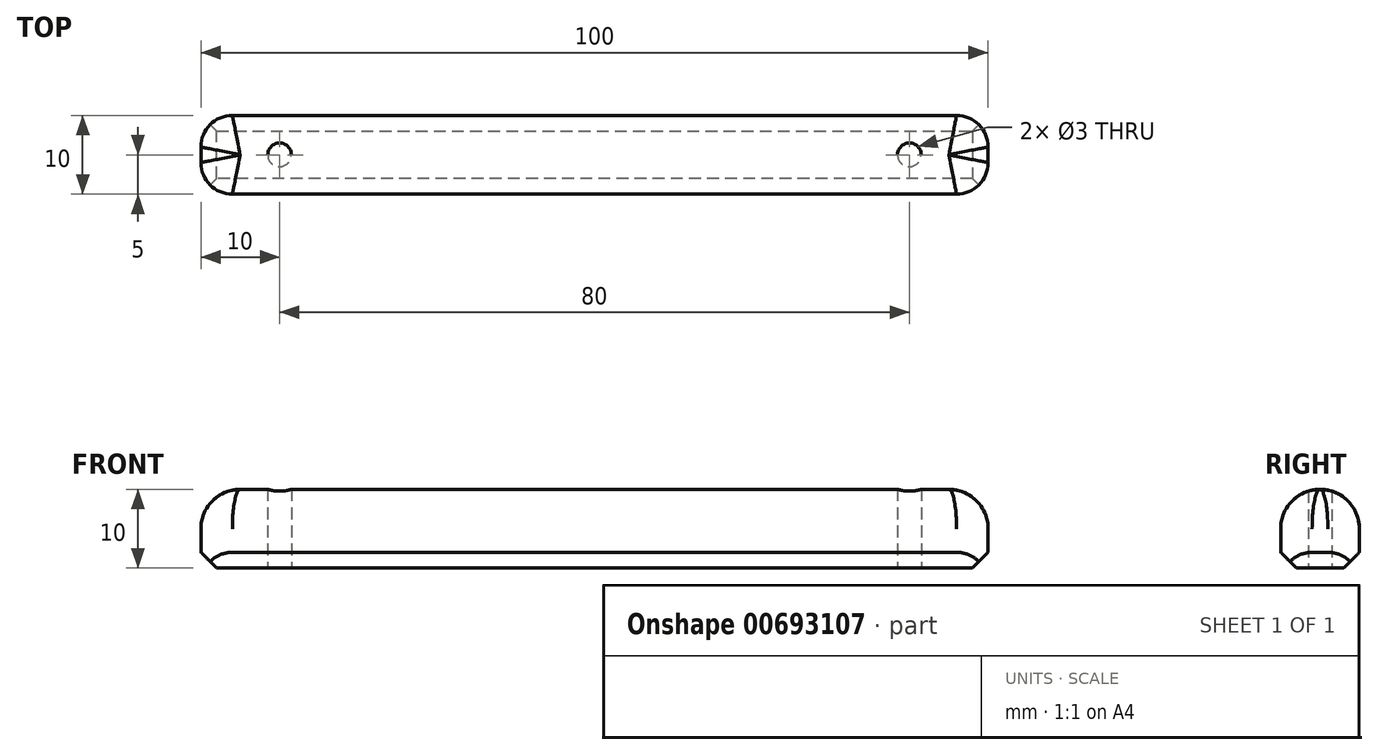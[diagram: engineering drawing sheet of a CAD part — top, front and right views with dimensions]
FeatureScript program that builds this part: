
annotation { "Feature Type Name" : "Feature", "Feature Type Description" : "" }
export const myFeature = defineFeature(function(context is Context, id is Id, definition is map)
    precondition{}
    {
        {
            var Q0;
            Q0=qCreatedBy(makeId("Top.planeOp"),FACE);
            var sketch = newSketch(context, id + "F0", { "sketchPlane" : qUnion([Q0])});
            skLineSegment(sketch, "E0.bottom", {"start": v(-50, 5) * mm, "end": v(50, 5) * mm});
            skLineSegment(sketch, "E0.top", {"start": v(-50, -5) * mm, "end": v(50, -5) * mm});
            skLineSegment(sketch, "E0.left", {"start": v(-50, 5) * mm, "end": v(-50, -5) * mm});
            skLineSegment(sketch, "E0.right", {"start": v(50, 5) * mm, "end": v(50, -5) * mm});
            skPoint(sketch, "E0.middle", {"position": v(0, 0) * mm});
            skSolve(sketch);
        }
        {
            var Q0;
            Q0 = qSketchRegion(id + "F0", true);
            extrude(context, id + "F1", {"entities" : qUnion([Q0]), "depth" : 10 * mm, "offsetDistance" : 25 * mm});
        }
        {
            var Q0;
            Q0=qCreatedBy(makeId("Top.planeOp"),FACE);
            var sketch = newSketch(context, id + "F2", { "sketchPlane" : qUnion([Q0])});
            skCircle(sketch, "E1", {"center": v(-40, 0) * mm, "radius": 1.5 * mm});
            skCircle(sketch, "E2", {"center": v(40, 0) * mm, "radius": 1.5 * mm});
            skSolve(sketch);
        }
        {
            var Q0;
            Q0 = qSketchRegion(id + "F2", true);
            extrude(context, id + "F3", {"entities" : qUnion([Q0]), "operationType" : NewBodyOperationType.REMOVE, "depth" : 10 * mm, "offsetDistance" : 25 * mm});
        }
        {
            var Q0;
            Q0=makeQuery(id+"F1.opExtrude","CAP_EDGE",EDGE,{"disambiguationData":[OSD([sQuery(id+"F0.wireOp",EDGE,"E0.top")])],"isStart":true});
            var Q1;
            Q1=makeQuery(id+"F1.opExtrude","CAP_EDGE",EDGE,{"disambiguationData":[OSD([sQuery(id+"F0.wireOp",EDGE,"E0.bottom")])],"isStart":true});
            var Q2;
            Q2=makeQuery(id+"F1.opExtrude","CAP_EDGE",EDGE,{"disambiguationData":[OSD([sQuery(id+"F0.wireOp",EDGE,"E0.left")])],"isStart":true});
            var Q3;
            Q3=makeQuery(id+"F1.opExtrude","CAP_EDGE",EDGE,{"disambiguationData":[OSD([sQuery(id+"F0.wireOp",EDGE,"E0.right")])],"isStart":true});
            chamfer(context, id + "F4", {"entities" : qUnion([Q0, Q1, Q2, Q3]), "width" : 2 * mm, "tangentPropagation" : true});
        }
        {
            var Q0;
            Q0=makeQuery(id+"F1.opExtrude","CAP_EDGE",EDGE,{"disambiguationData":[OSD([sQuery(id+"F0.wireOp",EDGE,"E0.top")])],"isStart":false});
            var Q1;
            Q1=makeQuery(id+"F1.opExtrude","CAP_EDGE",EDGE,{"disambiguationData":[OSD([sQuery(id+"F0.wireOp",EDGE,"E0.bottom")])],"isStart":false});
            var Q2;
            Q2=makeQuery(id+"F1.opExtrude","CAP_EDGE",EDGE,{"disambiguationData":[OSD([sQuery(id+"F0.wireOp",EDGE,"E0.left")])],"isStart":false});
            var Q3;
            Q3=makeQuery(id+"F1.opExtrude","CAP_EDGE",EDGE,{"disambiguationData":[OSD([sQuery(id+"F0.wireOp",EDGE,"E0.right")])],"isStart":false});
            fillet(context, id + "F5", {"entities" : qUnion([Q0, Q1, Q2, Q3]), "radius" : 5 * mm, "tangentPropagation" : true, "allowEdgeOverflow" : false});
        }
        {
            var Q0;
            Q0=makeQuery(id+"F1.opExtrude","SWEPT_EDGE",EDGE,{"disambiguationData":[OSD([sQuery(id+"F0.wireOp",EDGE,"E0.top"),sQuery(id+"F0.wireOp",EDGE,"E0.left")])]});
            var Q1;
            Q1=makeQuery(id+"F1.opExtrude","SWEPT_EDGE",EDGE,{"disambiguationData":[OSD([sQuery(id+"F0.wireOp",EDGE,"E0.bottom"),sQuery(id+"F0.wireOp",EDGE,"E0.left")])]});
            var Q2;
            Q2=makeQuery(id+"F1.opExtrude","SWEPT_EDGE",EDGE,{"disambiguationData":[OSD([sQuery(id+"F0.wireOp",EDGE,"E0.top"),sQuery(id+"F0.wireOp",EDGE,"E0.right")])]});
            var Q3;
            Q3=makeQuery(id+"F1.opExtrude","SWEPT_EDGE",EDGE,{"disambiguationData":[OSD([sQuery(id+"F0.wireOp",EDGE,"E0.bottom"),sQuery(id+"F0.wireOp",EDGE,"E0.right")])]});
            fillet(context, id + "F6", {"entities" : qUnion([Q0, Q1, Q2, Q3]), "radius" : 4 * mm, "tangentPropagation" : true, "allowEdgeOverflow" : false});
        }
    });
